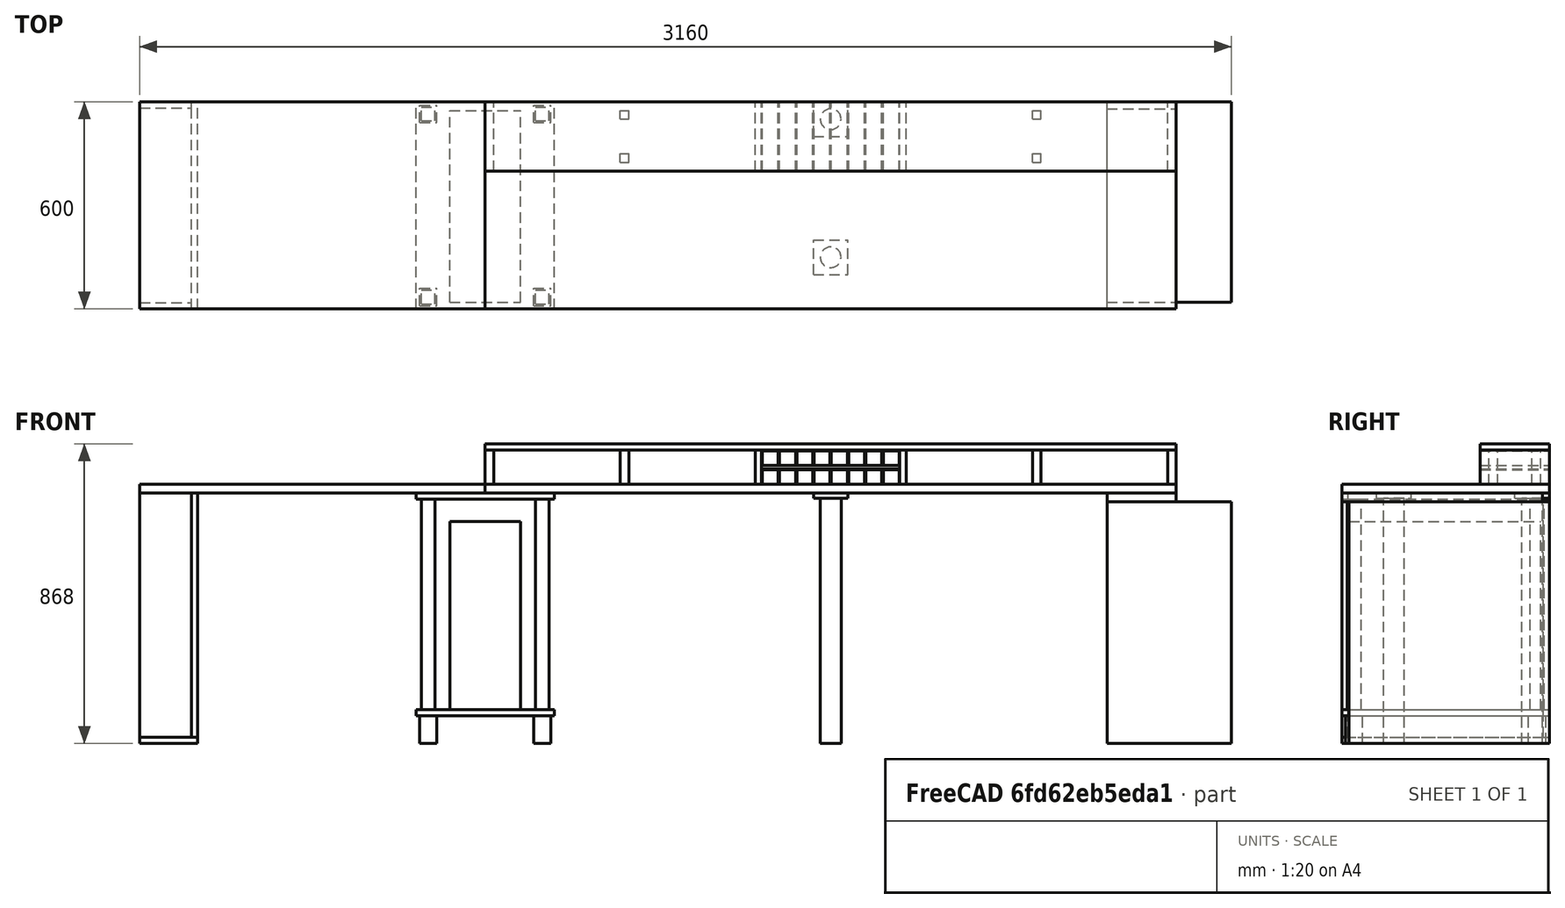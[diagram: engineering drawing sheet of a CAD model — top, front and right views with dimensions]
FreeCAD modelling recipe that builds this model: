
FCSTD DOCUMENT  (FreeCAD 0.15R4671 (Git))
Label: mesa
License: All rights reserved
LicenseURL: http://en.wikipedia.org/wiki/All_rights_reserved
objects: Part::Box×47, Part::Cylinder×2
note: 49 computed .brp shape members not serialized (recipe doc carries the construction recipe); baked Part::Feature solids carry a one-line shape summary decoded from their .brp

FEATURE [Part::Box] Box  label="Base"
  Height = 25
  Length = 2000
  Placement = pos=(0,0,725) rot=(0,0,1;0rad)
  Width = 600
FEATURE [Part::Box] Box001  label="Balda"
  Height = 18
  Length = 2000
  Placement = pos=(0,400,850) rot=(0,0,1;0rad)
  Width = 200
FEATURE [Part::Box] Box002  label="NZXTWhisper"
  Height = 545
  Length = 205
  Placement = pos=(-102.5,20,98) rot=(0,0,1;0rad)
  Width = 555
FEATURE [Part::Box] Box003  label="Leg100S_1"
  Height = 100
  Length = 25
  Placement = pos=(391,550,750) rot=(0,0,1;0rad)
  Width = 25
FEATURE [Part::Box] Box004  label="Leg100S_2"
  Height = 100
  Length = 25
  Placement = pos=(391,425,750) rot=(0,0,1;0rad)
  Width = 25
FEATURE [Part::Box] Box005  label="Leg100S_3"
  Height = 100
  Length = 25
  Placement = pos=(1584,550,750) rot=(0,0,1;0rad)
  Width = 25
FEATURE [Part::Box] Box006  label="Leg100S_4"
  Height = 100
  Length = 25
  Placement = pos=(1584,425,750) rot=(0,0,1;0rad)
  Width = 25
FEATURE [Part::Box] Box007  label="ElecStorageS_l"
  Height = 100
  Length = 18
  Placement = pos=(782,400,750) rot=(0,0,1;0rad)
  Width = 200
FEATURE [Part::Box] Box008  label="ElecStorageS_r"
  Height = 100
  Length = 18
  Placement = pos=(1200,400,750) rot=(0,0,1;0rad)
  Width = 200
FEATURE [Part::Box] Box009  label="ElecStorage_m"
  Height = 10
  Length = 400
  Placement = pos=(800,400,795) rot=(0,0,1;0rad)
  Width = 200
FEATURE [Part::Box] Box010  label="ElecBox_1b"
  Height = 42
  Length = 46
  Placement = pos=(802,400,750) rot=(0,0,1;0rad)
  Width = 200
FEATURE [Part::Box] Box011  label="ElecBox_2b"
  Height = 42
  Length = 46
  Placement = pos=(852,400,750) rot=(0,0,1;0rad)
  Width = 200
FEATURE [Part::Box] Box012  label="ElecBox_3b"
  Height = 42
  Length = 46
  Placement = pos=(902,400,750) rot=(0,0,1;0rad)
  Width = 200
FEATURE [Part::Box] Box013  label="ElecBox_4b"
  Height = 42
  Length = 46
  Placement = pos=(952,400,750) rot=(0,0,1;0rad)
  Width = 200
FEATURE [Part::Box] Box014  label="ElecBox_5b"
  Height = 42
  Length = 46
  Placement = pos=(1002,400,750) rot=(0,0,1;0rad)
  Width = 200
FEATURE [Part::Box] Box015  label="ElecBox_6b"
  Height = 42
  Length = 46
  Placement = pos=(1052,400,750) rot=(0,0,1;0rad)
  Width = 200
FEATURE [Part::Box] Box016  label="ElecBox_7b"
  Height = 42
  Length = 46
  Placement = pos=(1102,400,750) rot=(0,0,1;0rad)
  Width = 200
FEATURE [Part::Box] Box017  label="ElecBox_8b"
  Height = 42
  Length = 46
  Placement = pos=(1152,400,750) rot=(0,0,1;0rad)
  Width = 200
FEATURE [Part::Box] Box018  label="ElecBox_6t"
  Height = 42
  Length = 46
  Placement = pos=(1052,400,805) rot=(0,0,1;0rad)
  Width = 200
FEATURE [Part::Box] Box019  label="ElecBox_4t"
  Height = 42
  Length = 46
  Placement = pos=(952,400,805) rot=(0,0,1;0rad)
  Width = 200
FEATURE [Part::Box] Box020  label="ElecBox_7tt"
  Height = 42
  Length = 46
  Placement = pos=(1102,400,805) rot=(0,0,1;0rad)
  Width = 200
FEATURE [Part::Box] Box021  label="ElecBox_5t"
  Height = 42
  Length = 46
  Placement = pos=(1002,400,805) rot=(0,0,1;0rad)
  Width = 200
FEATURE [Part::Box] Box022  label="ElecBox_8t"
  Height = 42
  Length = 46
  Placement = pos=(1152,400,805) rot=(0,0,1;0rad)
  Width = 200
FEATURE [Part::Box] Box023  label="ElecBox_2t"
  Height = 42
  Length = 46
  Placement = pos=(852,400,805) rot=(0,0,1;0rad)
  Width = 200
FEATURE [Part::Box] Box024  label="ElecBox_3t"
  Height = 42
  Length = 46
  Placement = pos=(902,400,805) rot=(0,0,1;0rad)
  Width = 200
FEATURE [Part::Box] Box025  label="ElecBox_1t"
  Height = 42
  Length = 46
  Placement = pos=(802,400,805) rot=(0,0,1;0rad)
  Width = 200
FEATURE [Part::Box] Box026  label="Leg100R_l"
  Height = 100
  Length = 25
  Placement = pos=(0,400,750) rot=(0,0,1;0rad)
  Width = 200
FEATURE [Part::Box] Box027  label="Leg100R_r"
  Height = 100
  Length = 25
  Placement = pos=(1975,400,750) rot=(0,0,1;0rad)
  Width = 200
FEATURE [Part::Cylinder] Cylinder002  label="Leg710C_3"
  Angle = 360
  Height = 710
  Placement = pos=(1000,550,0) rot=(0,0,1;0rad)
  Radius = 30
FEATURE [Part::Cylinder] Cylinder003  label="Leg710C_4"
  Angle = 360
  Height = 710
  Placement = pos=(1000,150,0) rot=(0,0,1;0rad)
  Radius = 30
FEATURE [Part::Box] Box030  label="FixLeg710_3"
  Height = 15
  Length = 100
  Placement = pos=(950,500,710) rot=(0,0,1;0rad)
  Width = 100
FEATURE [Part::Box] Box031  label="FixLeg710_4"
  Height = 15
  Length = 100
  Placement = pos=(950,100,710) rot=(0,0,1;0rad)
  Width = 100
FEATURE [Part::Box] Box034  label="BaseAdd"
  Height = 25
  Length = 1000
  Placement = pos=(-1000,0,725) rot=(0,0,1;0rad)
  Width = 600
FEATURE [Part::Box] Box035  label="Leg725R"
  Height = 707
  Length = 18
  Placement = pos=(-850,0,18) rot=(0,0,1;0rad)
  Width = 600
FEATURE [Part::Box] Box036  label="IkeaALEX"
  Height = 700
  Length = 360
  Placement = pos=(1800,20,0) rot=(0,0,1;0rad)
  Width = 580
FEATURE [Part::Box] Box037  label="FixIkeaALEX"
  Height = 25
  Length = 200
  Placement = pos=(1800,0,700) rot=(0,0,1;0rad)
  Width = 580
FEATURE [Part::Box] Box038  label="FixAdd_t"
  Height = 18
  Length = 400
  Placement = pos=(-200,0,707) rot=(0,0,1;0rad)
  Width = 600
FEATURE [Part::Box] Box039  label="FixAdd_b"
  Height = 18
  Length = 400
  Placement = pos=(-200,0,80) rot=(0,0,1;0rad)
  Width = 600
FEATURE [Part::Box] Box041  label="Leg80S_1"
  Height = 80
  Length = 50
  Placement = pos=(-190,540,0) rot=(0,0,1;0rad)
  Width = 50
FEATURE [Part::Box] Box042  label="Leg80S_2"
  Height = 80
  Length = 50
  Placement = pos=(-190,10,0) rot=(0,0,1;0rad)
  Width = 50
FEATURE [Part::Box] Box043  label="Leg80S_3"
  Height = 80
  Length = 50
  Placement = pos=(140,540,0) rot=(0,0,1;0rad)
  Width = 50
FEATURE [Part::Box] Box044  label="Leg80S_4"
  Height = 80
  Length = 50
  Placement = pos=(140,10,0) rot=(0,0,1;0rad)
  Width = 50
FEATURE [Part::Box] Box045  label="Leg609S_1"
  Height = 609
  Length = 40
  Placement = pos=(-185,545,98) rot=(0,0,1;0rad)
  Width = 40
FEATURE [Part::Box] Box046  label="Leg609S_2"
  Height = 609
  Length = 40
  Placement = pos=(-185,15,98) rot=(0,0,1;0rad)
  Width = 40
FEATURE [Part::Box] Box047  label="Leg609S_3"
  Height = 609
  Length = 40
  Placement = pos=(145,545,98) rot=(0,0,1;0rad)
  Width = 40
FEATURE [Part::Box] Box048  label="Leg609S_4"
  Height = 609
  Length = 40
  Placement = pos=(145,15,98) rot=(0,0,1;0rad)
  Width = 40
FEATURE [Part::Box] Box049  label="Leg725R_f"
  Height = 707
  Length = 150
  Placement = pos=(-1000,0,18) rot=(0,0,1;0rad)
  Width = 18
FEATURE [Part::Box] Box050  label="Leg725R_r"
  Height = 707
  Length = 150
  Placement = pos=(-1000,582,18) rot=(0,0,1;0rad)
  Width = 18
FEATURE [Part::Box] Box051  label="Cube"
  Height = 18
  Length = 168
  Placement = pos=(-1000,0,0) rot=(0,0,1;0rad)
  Width = 600
